# Revit family: Washfountain_Lavatory-Bradley_Corp-WF2504-Type_A_Drain
name_source: partatom
category: Plumbing Fixtures
revit_build: Autodesk Revit MEP 2012 (Build: 20110309_2315(x64)
units: mm (PartAtom-declared; Revit-internal decimal feet)

## types (2) — shared parameters
ADA Compliant = Yes
Assembly Code = D2010300
Buy American Act = No
Cold Lavatory Inlet Primary = 1"
Cold Lavatory Inlet Primary Radius = 1/2"
Cold Lavatory Inlet Secondary = 1"
Cold Lavatory Inlet Secondary Radius = 1/2"
Description = Washfountain, 54" Semi Circular with 9" Deep Bowl
Drain = 2"
Drain Radius = 1"
Flow Type = 3.0 gal/min
Frequency = 50 Hz
Hot Lavatory Inlet Primary = 1"
Hot Lavatory Inlet Primary Radius = 1/2"
Hot Lavatory Inlet Secondary = 1"
Hot Lavatory Inlet Secondary Radius = 1/2"
Industry Standards = ANSI Z124.3, Z124.6 and ANSI/ICPA SS-1-2001
Manufacturer = Bradley Corp
MasterFormat Number = 22 42 16
MasterFormat Title = Commercial Lavatories and Sinks
Material Note = Other Terreon® colors available - See www.bradleycorp.com
Model = WF2504
OmniClass Table 21 Number = 21-04 20 10 60
OmniClass Table 21 Title = Plumbing Fixtures
OmniClass Table 23 Number = 23-31 13 00
OmniClass Table 23 Title = Sinks/Lavatories
Operating Water Pressure Range = 20 - 80 PSI
Pedestal Material = Stainless Steel - Bradley Corp - Satin
Product Tech Data URL - English = http://bradleycorp.com
Specifications URL = http://www.bradleycorp.com
URL = http://www.bradleycorp.com
Vent = 1 1/2"
Vent Radius = 3/4"
Version = 2.0
Voltage = 110 V
Warranty Information = Terreon® material warranted for ten years. All other components warranted for one year. This warranty does not cover installation or any other labor charges and does not apply to any units, which have been damaged by accident, abuse, improper installation, improper maintenance, or altered in any way.
Width = 54 "
zero-valued in all types: CWFU, HWFU, WFU

## per-type parameters (varying)
| type | Juvenile Height | Model ID | Pedestal Height | Rim Height | Secondary Supply Height | Sensor Module Height | Spray Head Height | Standard Height |
| Standard | No | 2 | 19 " | 29.5 " | 12 " | 42.25 " | 38.75 " | Yes |
| Juvenile | Yes | 1 | 15 " | 25.5 " | 8.25 " | 38.25 " | 34.75 " | No |

## geometry (parser evidence)
native form markers: Blend x18, Sweep x1
no freeform markers — native parametric forms only
